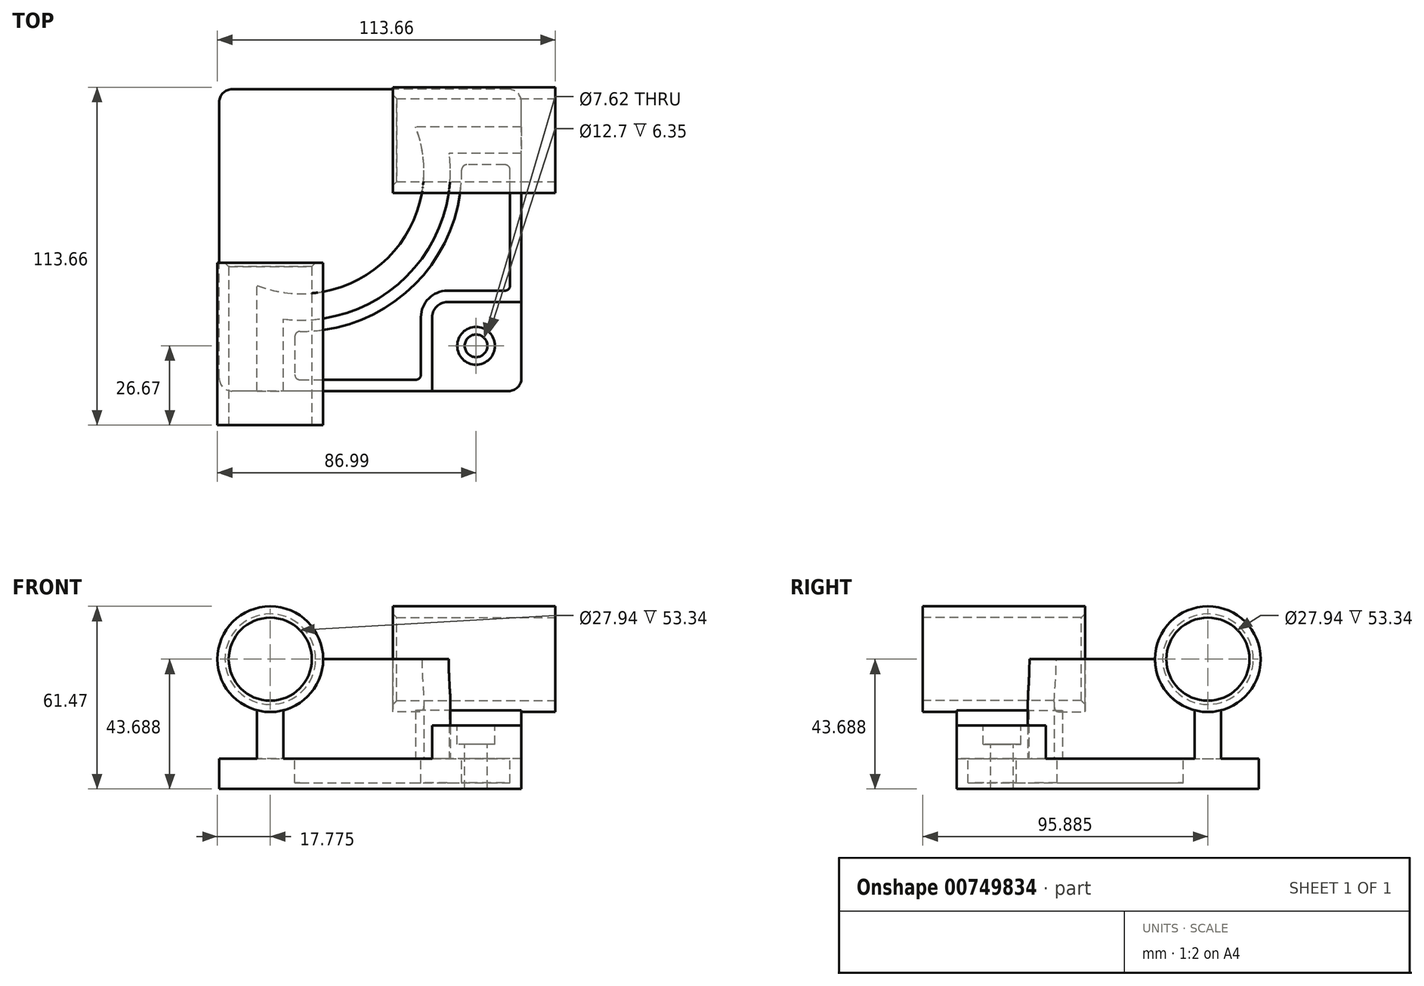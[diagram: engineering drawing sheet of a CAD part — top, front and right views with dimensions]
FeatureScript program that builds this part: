
annotation { "Feature Type Name" : "Feature", "Feature Type Description" : "" }
export const myFeature = defineFeature(function(context is Context, id is Id, definition is map)
    precondition{}
    {
        {
            var Q0;
            Q0=qCreatedBy(makeId("Top.planeOp"),FACE);
            var sketch = newSketch(context, id + "F0", { "sketchPlane" : qUnion([Q0])});
            skLineSegment(sketch, "E0.bottom", {"start": v(50.8, -50.8) * mm, "end": v(-50.8, -50.8) * mm});
            skLineSegment(sketch, "E0.top", {"start": v(50.8, 50.8) * mm, "end": v(-50.8, 50.8) * mm});
            skLineSegment(sketch, "E0.left", {"start": v(50.8, -50.8) * mm, "end": v(50.8, 50.8) * mm});
            skLineSegment(sketch, "E0.right", {"start": v(-50.8, -50.8) * mm, "end": v(-50.8, 50.8) * mm});
            skPoint(sketch, "E0.middle", {"position": v(0, 0) * mm});
            skSolve(sketch);
        }
        {
            var Q0;
            Q0=makeQuery(id+"F0.imprint","IMPRINT",FACE,{"disambiguationData":[TD([[makeQuery(id+"F0.imprint","IMPRINT",EDGE,{"derivedFrom":sQuery(id+"F0.wireOp",EDGE,"E0.bottom")}),-1.0]])]});
            extrude(context, id + "F1", {"entities" : qUnion([Q0]), "depth" : 10.16 * mm, "offsetDistance" : 25.4 * mm});
        }
        {
            var Q0;
            Q0=makeQuery(id+"F1.opExtrude","CAP_FACE",FACE,{"disambiguationData":[OSD([sQuery(id+"F0.wireOp",EDGE,"E0.bottom"),sQuery(id+"F0.wireOp",EDGE,"E0.top"),sQuery(id+"F0.wireOp",EDGE,"E0.left"),sQuery(id+"F0.wireOp",EDGE,"E0.right")])],"isStart":false});
            var sketch = newSketch(context, id + "F2", { "sketchPlane" : qUnion([Q0])});
            skLineSegment(sketch, "E1", {"start": v(-38.1, -50.8) * mm, "end": v(-38.1, -15.24) * mm});
            skLineSegment(sketch, "E2", {"start": v(50.8, 38.1) * mm, "end": v(15.24, 38.1) * mm});
            skArc(sketch, "E3", {"start": v(-38.1, -15.24) * mm, "mid": v(5.93, -5.93) * mm, "end": v(15.24, 38.1) * mm});
            skLineSegment(sketch, "E4.0", {"start": v(-29.2, -50.8) * mm, "end": v(-29.2, -26.54) * mm});
            skArc(sketch, "E4.1", {"start": v(-29.2, -26.54) * mm, "mid": v(12.21, -12.21) * mm, "end": v(26.54, 29.2) * mm});
            skLineSegment(sketch, "E4.2", {"start": v(50.8, 29.2) * mm, "end": v(26.54, 29.2) * mm});
            skLineSegment(sketch, "E5.0", {"start": v(50.8, -50.8) * mm, "end": v(50.8, 50.8) * mm});
            skLineSegment(sketch, "E6.0", {"start": v(50.8, -50.8) * mm, "end": v(-50.8, -50.8) * mm});
            skSolve(sketch);
        }
        {
            var Q0;
            {var subQ2=sQuery(id+"F2.wireOp",EDGE,"E1");Q0=makeQuery(id+"F2.imprint","IMPRINT",FACE,{"disambiguationData":[TD([[makeQuery(id+"F2.imprint","IMPRINT",EDGE,{"derivedFrom":subQ2}),-1.0]])]});}
            extrude(context, id + "F3", {"entities" : qUnion([Q0]), "operationType" : NewBodyOperationType.ADD, "depth" : 33.53 * mm, "offsetDistance" : 25.4 * mm});
        }
        {
            var Q0;
            Q0=makeQuery(id+"F3.boolean.opBoolean","MERGE",FACE,{"derivedFrom":[makeQuery(id+"F1.opExtrude","SWEPT_FACE",FACE,{"disambiguationData":[OSD([sQuery(id+"F0.wireOp",EDGE,"E0.bottom")])]}),makeQuery(id+"F3.opExtrude","SWEPT_FACE",FACE,{"disambiguationData":[OSD([sQuery(id+"F2.wireOp",EDGE,"E6.0")])]})]});
            var sketch = newSketch(context, id + "F4", { "sketchPlane" : qUnion([Q0])});
            skCircle(sketch, "E7", {"center": v(-33.65, 43.69) * mm, "radius": 17.78 * mm});
            skSolve(sketch);
        }
        {
            var Q0;
            {var subQ1=sQuery(id+"F2.wireOp",EDGE,"E6.0");var subQ6=makeQuery(id+"F3.opExtrude","CAP_EDGE",EDGE,{"disambiguationData":[OSD([subQ1])],"isStart":false});Q0=makeQuery(id+"F4.imprint","IMPRINT",FACE,{"disambiguationData":[TD([[makeQuery(id+"F4.imprint","IMPRINT",EDGE,{"derivedFrom":subQ6}),-1.0]])]});}
            var Q1;
            {var subQ1=sQuery(id+"F2.wireOp",EDGE,"E6.0");var subQ6=makeQuery(id+"F3.opExtrude","CAP_EDGE",EDGE,{"disambiguationData":[OSD([subQ1])],"isStart":false});Q1=makeQuery(id+"F4.imprint","IMPRINT",FACE,{"disambiguationData":[TD([[makeQuery(id+"F4.imprint","IMPRINT",EDGE,{"derivedFrom":subQ6}),1.0]])]});}
            extrude(context, id + "F5", {"entities" : qUnion([Q0, Q1]), "operationType" : NewBodyOperationType.ADD, "depth" : 11.43 * mm, "offsetDistance" : 25.4 * mm, "hasSecondDirection" : true, "secondDirectionOppositeDirection" : true, "secondDirectionDepth" : 43.18 * mm});
        }
        {
            var Q0;
            Q0=makeQuery(id+"F3.boolean.opBoolean","MERGE",FACE,{"derivedFrom":[makeQuery(id+"F1.opExtrude","SWEPT_FACE",FACE,{"disambiguationData":[OSD([sQuery(id+"F0.wireOp",EDGE,"E0.left")])]}),makeQuery(id+"F3.opExtrude","SWEPT_FACE",FACE,{"disambiguationData":[OSD([sQuery(id+"F2.wireOp",EDGE,"E5.0")])]})]});
            var sketch = newSketch(context, id + "F6", { "sketchPlane" : qUnion([Q0])});
            skCircle(sketch, "E8", {"center": v(33.65, 43.69) * mm, "radius": 17.78 * mm});
            skSolve(sketch);
        }
        {
            var Q0;
            {var subQ1=sQuery(id+"F2.wireOp",EDGE,"E5.0");var subQ6=makeQuery(id+"F3.opExtrude","CAP_EDGE",EDGE,{"disambiguationData":[OSD([subQ1])],"isStart":false});Q0=makeQuery(id+"F6.imprint","IMPRINT",FACE,{"disambiguationData":[TD([[makeQuery(id+"F6.imprint","IMPRINT",EDGE,{"derivedFrom":subQ6}),1.0]])]});}
            var Q1;
            {var subQ1=sQuery(id+"F2.wireOp",EDGE,"E5.0");var subQ6=makeQuery(id+"F3.opExtrude","CAP_EDGE",EDGE,{"disambiguationData":[OSD([subQ1])],"isStart":false});Q1=makeQuery(id+"F6.imprint","IMPRINT",FACE,{"disambiguationData":[TD([[makeQuery(id+"F6.imprint","IMPRINT",EDGE,{"derivedFrom":subQ6}),-1.0]])]});}
            extrude(context, id + "F7", {"entities" : qUnion([Q0, Q1]), "operationType" : NewBodyOperationType.ADD, "depth" : 11.43 * mm, "offsetDistance" : 25.4 * mm, "hasSecondDirection" : true, "secondDirectionOppositeDirection" : true, "secondDirectionDepth" : 43.18 * mm});
        }
        {
            var Q0;
            {var subQ0=sQuery(id+"F0.wireOp",EDGE,"E0.left");var subQ1=sQuery(id+"F0.wireOp",EDGE,"E0.bottom");Q0=makeQuery(id+"F3.boolean.opBoolean","SPLIT",FACE,{"disambiguationData":[TD([makeQuery(id+"F3.opExtrude","SWEPT_FACE",FACE,{"disambiguationData":[OSD([sQuery(id+"F2.wireOp",EDGE,"E4.0")])]})])],"derivedFrom":makeQuery(id+"F1.opExtrude","CAP_FACE",FACE,{"disambiguationData":[OSD([subQ1,sQuery(id+"F0.wireOp",EDGE,"E0.top"),subQ0,sQuery(id+"F0.wireOp",EDGE,"E0.right")])],"isStart":false})});}
            var sketch = newSketch(context, id + "F8", { "sketchPlane" : qUnion([Q0])});
            skLineSegment(sketch, "E9.bottom", {"start": v(50.8, -50.8) * mm, "end": v(20.83, -50.8) * mm});
            skLineSegment(sketch, "E9.top", {"start": v(50.8, -20.83) * mm, "end": v(20.83, -20.83) * mm});
            skLineSegment(sketch, "E9.left", {"start": v(50.8, -50.8) * mm, "end": v(50.8, -20.83) * mm});
            skLineSegment(sketch, "E9.right", {"start": v(20.83, -50.8) * mm, "end": v(20.83, -20.83) * mm});
            skSolve(sketch);
        }
        {
            var Q0;
            Q0=makeQuery(id+"F8.imprint","IMPRINT",FACE,{"disambiguationData":[TD([[makeQuery(id+"F8.imprint","IMPRINT",EDGE,{"derivedFrom":sQuery(id+"F8.wireOp",EDGE,"E9.bottom")}),-1.0]])]});
            extrude(context, id + "F9", {"entities" : qUnion([Q0]), "operationType" : NewBodyOperationType.ADD, "depth" : 11.18 * mm, "offsetDistance" : 25.4 * mm});
        }
        {
            var Q0;
            Q0=makeQuery(id+"F9.opExtrude","SWEPT_EDGE",EDGE,{"disambiguationData":[OSD([sQuery(id+"F8.wireOp",EDGE,"E9.top"),sQuery(id+"F8.wireOp",EDGE,"E9.right")])]});
            fillet(context, id + "F10", {"entities" : qUnion([Q0]), "radius" : 5.08 * mm, "tangentPropagation" : true, "allowEdgeOverflow" : false});
        }
        {
            var Q0;
            {var subQ0=sQuery(id+"F0.wireOp",EDGE,"E0.left");var subQ1=sQuery(id+"F0.wireOp",EDGE,"E0.bottom");Q0=makeQuery(id+"F3.boolean.opBoolean","SPLIT",FACE,{"disambiguationData":[TD([makeQuery(id+"F3.opExtrude","SWEPT_FACE",FACE,{"disambiguationData":[OSD([sQuery(id+"F2.wireOp",EDGE,"E4.0")])]})])],"derivedFrom":makeQuery(id+"F1.opExtrude","CAP_FACE",FACE,{"disambiguationData":[OSD([subQ1,sQuery(id+"F0.wireOp",EDGE,"E0.top"),subQ0,sQuery(id+"F0.wireOp",EDGE,"E0.right")])],"isStart":false})});}
            var sketch = newSketch(context, id + "F11", { "sketchPlane" : qUnion([Q0])});
            skLineSegment(sketch, "E10.0", {"start": v(-25.4, -30.66) * mm, "end": v(-25.4, -46.99) * mm});
            skArc(sketch, "E10.1", {"start": v(30.66, 25.4) * mm, "mid": v(14.9, -14.9) * mm, "end": v(-25.4, -30.66) * mm});
            skLineSegment(sketch, "E10.2", {"start": v(-25.4, -46.99) * mm, "end": v(17.02, -46.99) * mm});
            skLineSegment(sketch, "E10.3", {"start": v(46.99, 25.4) * mm, "end": v(30.66, 25.4) * mm});
            skLineSegment(sketch, "E10.4", {"start": v(17.02, -46.99) * mm, "end": v(17.02, -25.9) * mm});
            skArc(sketch, "E10.5", {"start": v(17.02, -25.9) * mm, "mid": v(19.62, -19.62) * mm, "end": v(25.9, -17.02) * mm});
            skLineSegment(sketch, "E10.6", {"start": v(25.9, -17.02) * mm, "end": v(46.99, -17.02) * mm});
            skLineSegment(sketch, "E10.7", {"start": v(46.99, -17.02) * mm, "end": v(46.99, 25.4) * mm});
            skSolve(sketch);
        }
        {
            var Q0;
            Q0=makeQuery(id+"F11.imprint","IMPRINT",FACE,{"disambiguationData":[TD([[makeQuery(id+"F11.imprint","IMPRINT",EDGE,{"derivedFrom":sQuery(id+"F11.wireOp",EDGE,"E10.0")}),1.0]])]});
            extrude(context, id + "F12", {"entities" : qUnion([Q0]), "operationType" : NewBodyOperationType.REMOVE, "oppositeDirection" : true, "depth" : 8.13 * mm, "offsetDistance" : 25.4 * mm});
        }
        {
            var Q0;
            Q0=makeQuery(id+"F9.opExtrude","CAP_FACE",FACE,{"disambiguationData":[OSD([sQuery(id+"F8.wireOp",EDGE,"E9.bottom"),sQuery(id+"F8.wireOp",EDGE,"E9.top"),sQuery(id+"F8.wireOp",EDGE,"E9.left"),sQuery(id+"F8.wireOp",EDGE,"E9.right")])],"isStart":false});
            var sketch = newSketch(context, id + "F13", { "sketchPlane" : qUnion([Q0])});
            skCircle(sketch, "E11", {"center": v(35.56, -35.56) * mm, "radius": 9.43 * mm});
            skSolve(sketch);
        }
        {
            var Q0;
            Q0=sQuery(id+"F13.wireOp",VERTEX,"E11.center");
            var Q1;
            Q1=makeQuery(id+"F1.opExtrude","SWEPT_BODY",BODY,{"disambiguationData":[OSD([sQuery(id+"F0.wireOp",EDGE,"E0.bottom"),sQuery(id+"F0.wireOp",EDGE,"E0.top"),sQuery(id+"F0.wireOp",EDGE,"E0.left"),sQuery(id+"F0.wireOp",EDGE,"E0.right")])]});
            hole(context, id + "F14", {"style" : HoleStyle.C_BORE, "endStyle" : HoleEndStyle.THROUGH, "holeDiameter" : 7.62 * mm, "cBoreDiameter" : 12.7 * mm, "cBoreDepth" : 6.35 * mm, "majorDiameter" : 6.35 * mm, "isTappedThrough" : true, "tappedDepth" : 12.7 * mm, "tapClearance" : 3, "locations" : qUnion([Q0]), "scope" : qUnion([Q1])});
        }
        {
            var Q0;
            Q0=makeQuery(id+"F12.boolean.opBoolean","COPY",EDGE,{"derivedFrom":makeQuery(id+"F12.opExtrude","SWEPT_EDGE",EDGE,{"disambiguationData":[OSD([sQuery(id+"F11.wireOp",EDGE,"E10.0"),sQuery(id+"F11.wireOp",EDGE,"E10.2")])]})});
            var Q1;
            Q1=makeQuery(id+"F12.boolean.opBoolean","COPY",EDGE,{"derivedFrom":makeQuery(id+"F12.opExtrude","SWEPT_EDGE",EDGE,{"disambiguationData":[OSD([sQuery(id+"F11.wireOp",EDGE,"E10.0"),sQuery(id+"F11.wireOp",EDGE,"E10.1")])]})});
            var Q2;
            Q2=makeQuery(id+"F12.boolean.opBoolean","COPY",EDGE,{"derivedFrom":makeQuery(id+"F12.opExtrude","SWEPT_EDGE",EDGE,{"disambiguationData":[OSD([sQuery(id+"F11.wireOp",EDGE,"E10.1"),sQuery(id+"F11.wireOp",EDGE,"E10.3")])]})});
            var Q3;
            Q3=makeQuery(id+"F12.boolean.opBoolean","COPY",EDGE,{"derivedFrom":makeQuery(id+"F12.opExtrude","SWEPT_EDGE",EDGE,{"disambiguationData":[OSD([sQuery(id+"F11.wireOp",EDGE,"E10.3"),sQuery(id+"F11.wireOp",EDGE,"E10.7")])]})});
            var Q4;
            Q4=makeQuery(id+"F12.boolean.opBoolean","COPY",EDGE,{"derivedFrom":makeQuery(id+"F12.opExtrude","SWEPT_EDGE",EDGE,{"disambiguationData":[OSD([sQuery(id+"F11.wireOp",EDGE,"E10.6"),sQuery(id+"F11.wireOp",EDGE,"E10.7")])]})});
            var Q5;
            Q5=makeQuery(id+"F12.boolean.opBoolean","COPY",EDGE,{"derivedFrom":makeQuery(id+"F12.opExtrude","SWEPT_EDGE",EDGE,{"disambiguationData":[OSD([sQuery(id+"F11.wireOp",EDGE,"E10.2"),sQuery(id+"F11.wireOp",EDGE,"E10.4")])]})});
            fillet(context, id + "F15", {"entities" : qUnion([Q0, Q1, Q2, Q3, Q4, Q5]), "radius" : 1.78 * mm, "tangentPropagation" : true, "allowEdgeOverflow" : false});
        }
        {
            var Q0;
            Q0=makeQuery(id+"F5.opExtrude","CAP_FACE",FACE,{"disambiguationData":[OSD([sQuery(id+"F4.wireOp",EDGE,"E7")])],"isStart":false});
            var sketch = newSketch(context, id + "F16", { "sketchPlane" : qUnion([Q0])});
            skCircle(sketch, "E12", {"center": v(-33.65, 43.69) * mm, "radius": 13.97 * mm});
            skSolve(sketch);
        }
        {
            var Q0;
            Q0=makeQuery(id+"F16.imprint","IMPRINT",FACE,{"disambiguationData":[TD([[makeQuery(id+"F16.imprint","IMPRINT",EDGE,{"derivedFrom":sQuery(id+"F16.wireOp",EDGE,"E12")}),1.0]])]});
            extrude(context, id + "F17", {"entities" : qUnion([Q0]), "operationType" : NewBodyOperationType.REMOVE, "oppositeDirection" : true, "depth" : 86.87 * mm, "offsetDistance" : 25.4 * mm});
        }
        {
            var Q0;
            Q0=makeQuery(id+"F7.opExtrude","CAP_FACE",FACE,{"disambiguationData":[OSD([sQuery(id+"F6.wireOp",EDGE,"E8")])],"isStart":false});
            var sketch = newSketch(context, id + "F18", { "sketchPlane" : qUnion([Q0])});
            skCircle(sketch, "E13", {"center": v(33.65, 43.69) * mm, "radius": 13.97 * mm});
            skSolve(sketch);
        }
        {
            var Q0;
            Q0=makeQuery(id+"F18.imprint","IMPRINT",FACE,{"disambiguationData":[TD([[makeQuery(id+"F18.imprint","IMPRINT",EDGE,{"derivedFrom":sQuery(id+"F18.wireOp",EDGE,"E13")}),1.0]])]});
            extrude(context, id + "F19", {"entities" : qUnion([Q0]), "operationType" : NewBodyOperationType.REMOVE, "oppositeDirection" : true, "depth" : 107.7 * mm, "offsetDistance" : 25.4 * mm});
        }
        {
            var Q0;
            Q0=makeQuery(id+"F19.boolean.opBoolean","COPY",EDGE,{"derivedFrom":makeQuery(id+"F19.opExtrude","CAP_EDGE",EDGE,{"disambiguationData":[OSD([sQuery(id+"F18.wireOp",EDGE,"E13")])],"isStart":true})});
            var Q1;
            Q1=makeQuery(id+"F17.boolean.opBoolean","COPY",EDGE,{"derivedFrom":makeQuery(id+"F17.opExtrude","CAP_EDGE",EDGE,{"disambiguationData":[OSD([sQuery(id+"F16.wireOp",EDGE,"E12")])],"isStart":true})});
            var Q2;
            Q2=makeQuery(id+"F19.boolean.opBoolean","INTERSECT",EDGE,{"derivedFrom":[makeQuery(id+"F7.opExtrude","CAP_FACE",FACE,{"disambiguationData":[OSD([sQuery(id+"F6.wireOp",EDGE,"E8")])],"isStart":true}),makeQuery(id+"F19.opExtrude","SWEPT_FACE",FACE,{"disambiguationData":[OSD([sQuery(id+"F18.wireOp",EDGE,"E13")])]})]});
            var Q3;
            Q3=makeQuery(id+"F17.boolean.opBoolean","INTERSECT",EDGE,{"derivedFrom":[makeQuery(id+"F5.opExtrude","CAP_FACE",FACE,{"disambiguationData":[OSD([sQuery(id+"F4.wireOp",EDGE,"E7")])],"isStart":true}),makeQuery(id+"F17.opExtrude","SWEPT_FACE",FACE,{"disambiguationData":[OSD([sQuery(id+"F16.wireOp",EDGE,"E12")])]})]});
            chamfer(context, id + "F20", {"entities" : qUnion([Q0, Q1, Q2, Q3]), "width" : 1.27 * mm, "tangentPropagation" : true});
        }
        {
            var Q0;
            Q0=makeQuery(id+"F9.boolean.opBoolean","MERGE",EDGE,{"derivedFrom":[makeQuery(id+"F1.opExtrude","SWEPT_EDGE",EDGE,{"disambiguationData":[OSD([sQuery(id+"F0.wireOp",EDGE,"E0.bottom"),sQuery(id+"F0.wireOp",EDGE,"E0.left")])]}),makeQuery(id+"F9.opExtrude","SWEPT_EDGE",EDGE,{"disambiguationData":[OSD([sQuery(id+"F8.wireOp",EDGE,"E9.bottom"),sQuery(id+"F8.wireOp",EDGE,"E9.left")])]})]});
            var Q1;
            Q1=makeQuery(id+"F1.opExtrude","SWEPT_EDGE",EDGE,{"disambiguationData":[OSD([sQuery(id+"F0.wireOp",EDGE,"E0.top"),sQuery(id+"F0.wireOp",EDGE,"E0.left")])]});
            var Q2;
            Q2=makeQuery(id+"F1.opExtrude","SWEPT_EDGE",EDGE,{"disambiguationData":[OSD([sQuery(id+"F0.wireOp",EDGE,"E0.top"),sQuery(id+"F0.wireOp",EDGE,"E0.right")])]});
            var Q3;
            Q3=makeQuery(id+"F1.opExtrude","SWEPT_EDGE",EDGE,{"disambiguationData":[OSD([sQuery(id+"F0.wireOp",EDGE,"E0.bottom"),sQuery(id+"F0.wireOp",EDGE,"E0.right")])]});
            fillet(context, id + "F21", {"entities" : qUnion([Q0, Q1, Q2, Q3]), "radius" : 4.32 * mm, "tangentPropagation" : true, "allowEdgeOverflow" : false});
        }
    });
